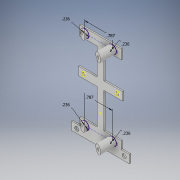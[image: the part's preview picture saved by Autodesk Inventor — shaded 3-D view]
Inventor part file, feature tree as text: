
AUTODESK INVENTOR PART (.ipt)
format: ipt  version: 2018 (Build 220112000, 112)  size: 287,232 bytes
history: native  units: in
note: dims shown in document units (in); Inventor stores cm internally (conversion verified against a paired STEP export)
features: extrude x11, sketch x9
ambient origin geometry x8: Origin, YZ Plane, XZ Plane, XY Plane, X Axis, Y Axis, Z Axis, Center Point
bodies: Solid1 (feature_tree)
feature tree (20):
  extrude  "Extrusion1"  Depth=1.2598in
  extrude  "Extrusion2"  TaperAngle=0.0deg  [1 undecoded]
  extrude  "Extrusion3"  Depth=0.2362in
  sketch  "Sketch5"  dims[d7=0.0in d8=0.0394in d9=0.0in]
  extrude  "Extrusion5"  Depth=0.0394in TaperAngle=0.0deg
  extrude  "Extrusion6"  Depth=0.6791in
  sketch  "Sketch8"  dims[d14=0.6791in d15=0.1181in]
  extrude  "Extrusion9"  Depth=0.1181in
  extrude  "Extrusion14"  Depth=0.1181in
  extrude  "Extrusion11"  Depth=0.4823in
  extrude  "Extrusion12"  Depth=0.1181in
  extrude  "Extrusion13"  Depth=0.1969in TaperAngle=0.0deg
  extrude  "Extrusion15"  Depth=2.2835in
  sketch  "Sketch1"  dims[d0=0.1969in d2=1.2598in]
  sketch  "Sketch2"  dims[d3=0.2362in d4=0.0in]
  sketch  "Sketch4"  dims[d5=1.6535in d6=0.2362in]
  sketch  "Sketch6"  dims[d10=1.3583in d13=0.6791in]
  sketch  "Sketch9"  dims[d16=0.1181in d17=0.9646in]
  sketch  "Sketch10"  dims[d18=0.4823in d19=0.4823in]
  sketch  "Sketch12"  dims[d20=0.1181in d21=0.1181in d22=0.0787in d23=0.0in d28=2.2835in d29=0.1969in d30=0.0in d31=0.0in d32=0.1969in d33=1.1811in d34=1.1811in d35=0.2756in d36=0.2756in d37=0.0787in d38=0.0787in d39=0.0787in d40=0.0787in d41=0.9055in d42=0.9055in d43=0.4528in d44=0.4528in d45=0.4528in d46=0.4528in d47=0.0394in d48=0.0in d52=0.2362in d55=0.2362in d57=0.0787in d58=0.0in d59=0.2362in d60=0.2362in d61=0.2362in d62=0.2362in d63=0.0787in d64=0.0in d65=1.4567in d66=1.4567in d72=0.4604in d73=0.25in d74=0.0in d77=3.0in d78=0.0in d79=0.0394in d80=0.0in d81=0.9055in d82=2.2835in d83=0.1293in d84=0.1293in d85=0.1893in d86=0.1893in d87=0.0787in d88=0.0787in d89=0.0787in d90=0.0787in d91=0.1181in d92=0.0in d97=0.2362in d98=0.7874in d99=0.2362in d100=0.7874in d101=0.4724in d102=0.0in d103=0.0787in d104=0.0787in d105=0.9075in d106=0.0787in d110=0.0787in d111=0.0787in d112=0.9075in d113=0.0787in d114=0.1969in d115=0.0in]
note: 1 required parameter value undecoded (feature->parameter linkage not recoverable at this tier; creation-order binding heuristic only, values carry confidence <= 0.55)
